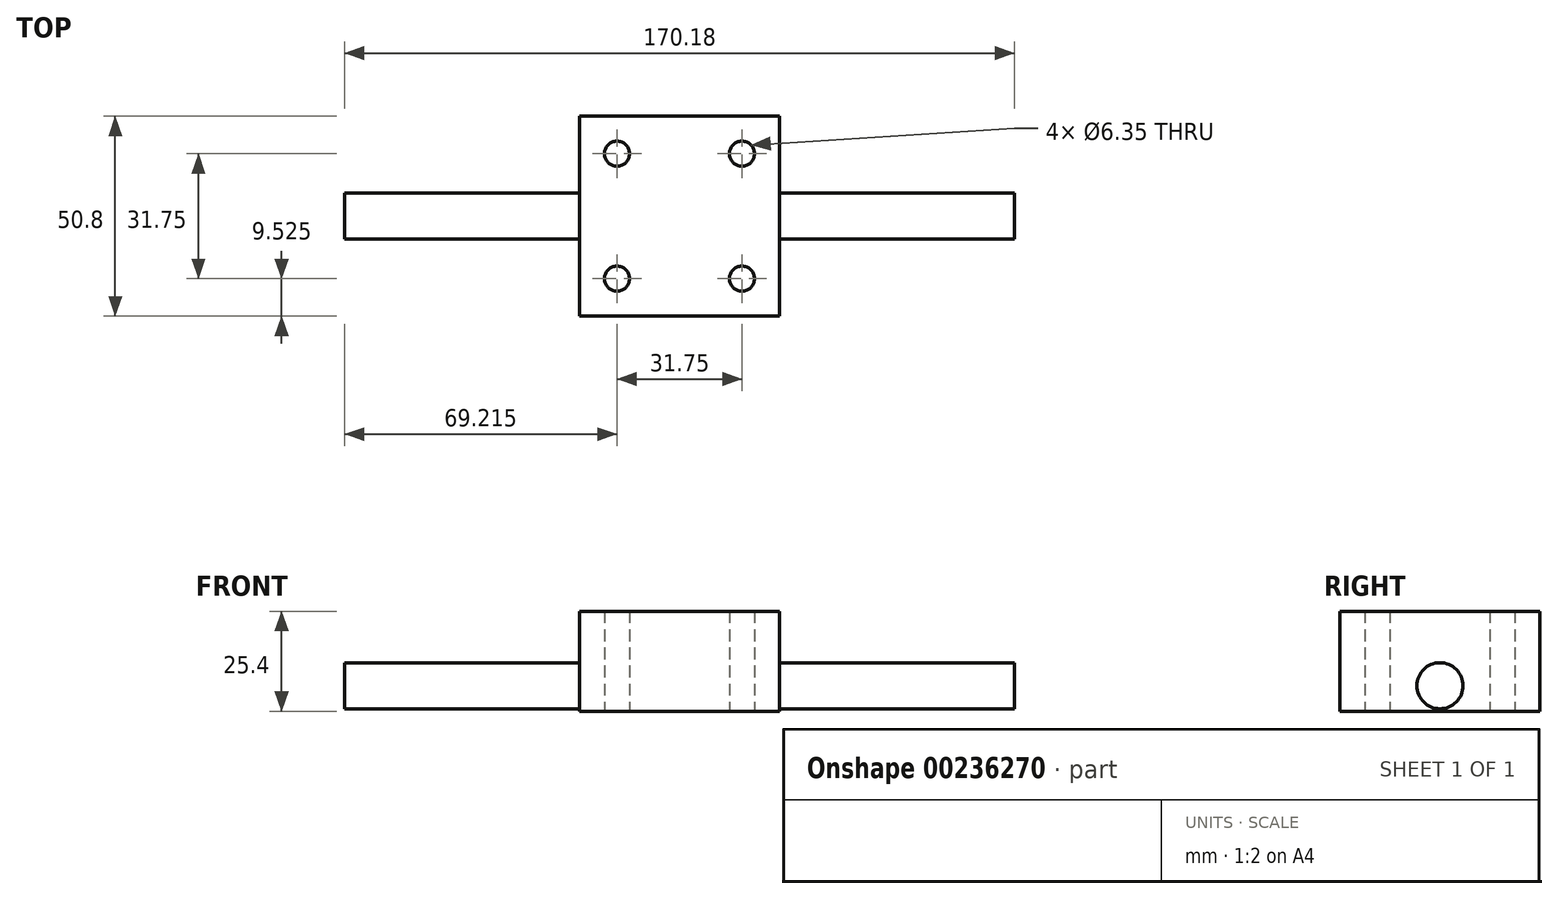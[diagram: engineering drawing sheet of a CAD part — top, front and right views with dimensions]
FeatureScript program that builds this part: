
annotation { "Feature Type Name" : "Feature", "Feature Type Description" : "" }
export const myFeature = defineFeature(function(context is Context, id is Id, definition is map)
    precondition{}
    {
        {
            var Q0;
            Q0=qCreatedBy(makeId("Top.planeOp"),FACE);
            var sketch = newSketch(context, id + "F0", { "sketchPlane" : qUnion([Q0])});
            skLineSegment(sketch, "E0.bottom", {"start": v(-25.4, 25.4) * mm, "end": v(25.4, 25.4) * mm});
            skLineSegment(sketch, "E0.top", {"start": v(-25.4, -25.4) * mm, "end": v(25.4, -25.4) * mm});
            skLineSegment(sketch, "E0.left", {"start": v(-25.4, 25.4) * mm, "end": v(-25.4, -25.4) * mm});
            skLineSegment(sketch, "E0.right", {"start": v(25.4, 25.4) * mm, "end": v(25.4, -25.4) * mm});
            skPoint(sketch, "E0.middle", {"position": v(0, 0) * mm});
            skCircle(sketch, "E1", {"center": v(-15.88, 15.88) * mm, "radius": 3.18 * mm});
            skCircle(sketch, "E2.MirrorC", {"center": v(15.88, 15.88) * mm, "radius": 3.18 * mm});
            skCircle(sketch, "E3.MirrorC", {"center": v(-15.88, -15.88) * mm, "radius": 3.18 * mm});
            skCircle(sketch, "E4.MirrorC", {"center": v(15.88, -15.88) * mm, "radius": 3.18 * mm});
            skSolve(sketch);
        }
        {
            var Q0;
            Q0 = qSketchRegion(id + "F0", true);
            extrude(context, id + "F1", {"entities" : qUnion([Q0]), "endBound" : BoundingType.SYMMETRIC, "depth" : 25.4 * mm});
        }
        {
            var Q0;
            Q0=qCreatedBy(makeId("Right.planeOp"),FACE);
            var sketch = newSketch(context, id + "F2", { "sketchPlane" : qUnion([Q0])});
            skCircle(sketch, "E5", {"center": v(0, -6.2) * mm, "radius": 5.85 * mm});
            skSolve(sketch);
        }
        {
            var Q0;
            Q0 = qSketchRegion(id + "F2", true);
            extrude(context, id + "F3", {"entities" : qUnion([Q0]), "operationType" : NewBodyOperationType.ADD, "depth" : 85.1 * mm});
        }
        {
            var Q0;
            Q0=makeQuery(id+"F1.opExtrude","SWEPT_BODY",BODY,{"disambiguationData":[OSD([sQuery(id+"F0.wireOp",EDGE,"E0.bottom"),sQuery(id+"F0.wireOp",EDGE,"E0.top"),sQuery(id+"F0.wireOp",EDGE,"E0.left"),sQuery(id+"F0.wireOp",EDGE,"E0.right"),sQuery(id+"F0.wireOp",EDGE,"E1"),sQuery(id+"F0.wireOp",EDGE,"2OjvseLX-bFbF-YJiS-uXVr-pNXyVovP3Xth"),sQuery(id+"F0.wireOp",EDGE,"Rn9LICby-feHb-zHKT-spQx-VyExxmWUtG9Z"),sQuery(id+"F0.wireOp",EDGE,"jDPRmAkI-vmGr-EVNM-SBit-r3bhJBwAZ531")])]});
            var Q1;
            Q1=qCreatedBy(makeId("Right.planeOp"),FACE);
            mirror(context, id + "F4", {"operationType" : NewBodyOperationType.ADD, "entities" : qUnion([Q0]), "mirrorPlane" : qUnion([Q1])});
        }
    });
